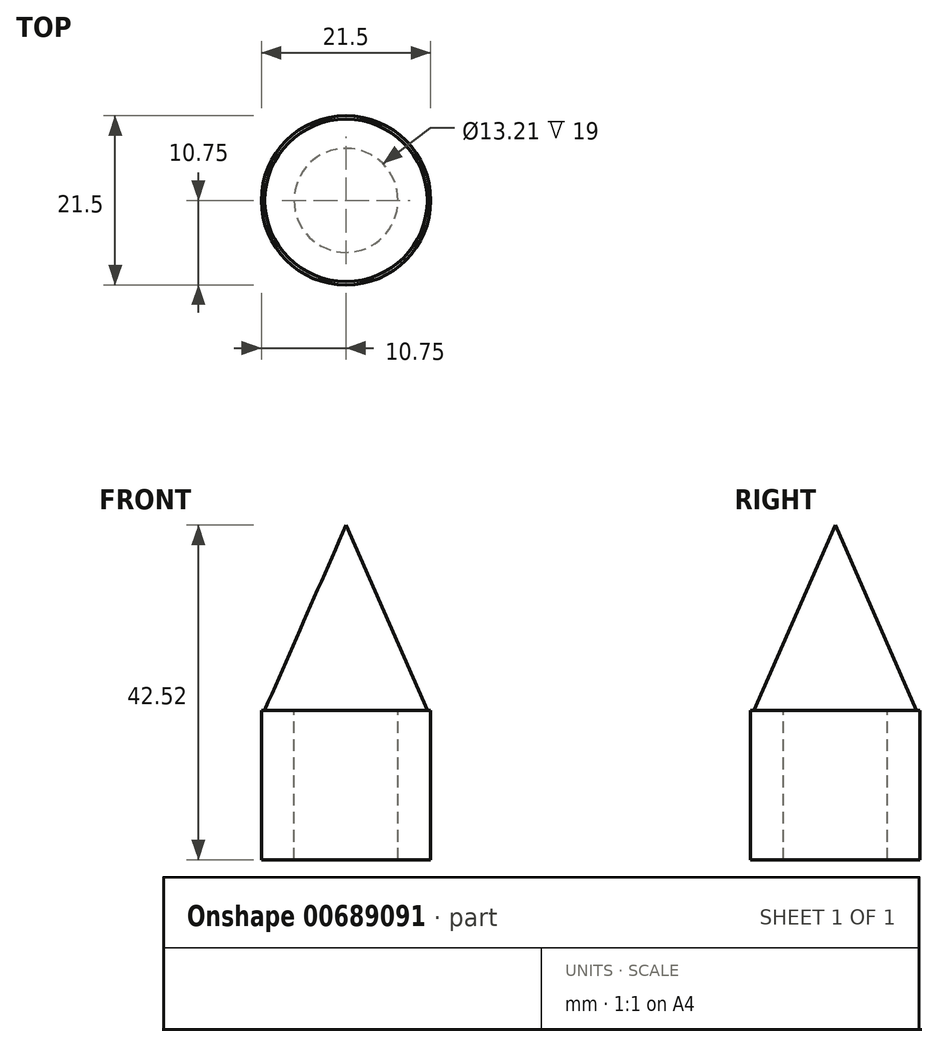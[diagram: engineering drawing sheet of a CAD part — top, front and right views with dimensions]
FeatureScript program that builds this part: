
annotation { "Feature Type Name" : "Feature", "Feature Type Description" : "" }
export const myFeature = defineFeature(function(context is Context, id is Id, definition is map)
    precondition{}
    {
        {
            var Q0;
            Q0=qCreatedBy(makeId("Top.planeOp"),FACE);
            var sketch = newSketch(context, id + "F0", { "sketchPlane" : qUnion([Q0])});
            skCircle(sketch, "E0", {"center": v(0, 0) * mm, "radius": 10.75 * mm});
            skCircle(sketch, "E1", {"center": v(0, 0) * mm, "radius": 6.6 * mm});
            skSolve(sketch);
        }
        {
            var Q0;
            Q0=makeQuery(id+"F0.imprint","IMPRINT",FACE,{"disambiguationData":[TD([[makeQuery(id+"F0.imprint","IMPRINT",EDGE,{"derivedFrom":sQuery(id+"F0.wireOp",EDGE,"E0")}),1.0]])]});
            extrude(context, id + "F1", {"entities" : qUnion([Q0]), "oppositeDirection" : true, "depth" : 19 * mm, "offsetDistance" : 25 * mm});
        }
        {
            var Q0;
            Q0=qCreatedBy(makeId("Right.planeOp"),FACE);
            var sketch = newSketch(context, id + "F2", { "sketchPlane" : qUnion([Q0])});
            skLineSegment(sketch, "E2", {"start": v(0, 0) * mm, "end": v(0, 23.52) * mm});
            skLineSegment(sketch, "E3", {"start": v(0, 23.52) * mm, "end": v(-10.32, 0) * mm});
            skLineSegment(sketch, "E4", {"start": v(-10.32, 0) * mm, "end": v(0, 0) * mm});
            skSolve(sketch);
        }
        {
            var Q0;
            Q0=qCreatedBy(makeId("Right.planeOp"),FACE);
            var sketch = newSketch(context, id + "F3", { "sketchPlane" : qUnion([Q0])});
            skLineSegment(sketch, "E5", {"start": v(0, 0) * mm, "end": v(0, -16.45) * mm});
            skSolve(sketch);
        }
        {
            var Q0;
            Q0=makeQuery(id+"F2.imprint","IMPRINT",FACE,{"disambiguationData":[TD([[makeQuery(id+"F2.imprint","IMPRINT",EDGE,{"derivedFrom":sQuery(id+"F2.wireOp",EDGE,"E2")}),1.0]])]});
            var Q1;
            Q1=sQuery(id+"F3.wireOp",EDGE,"E5");
            revolve(context, id + "F4", {"operationType" : NewBodyOperationType.ADD, "entities" : qUnion([Q0]), "axis" : qUnion([Q1]), "revolveType" : RevolveType.SYMMETRIC, "angle" : 360 * degree});
        }
    });
